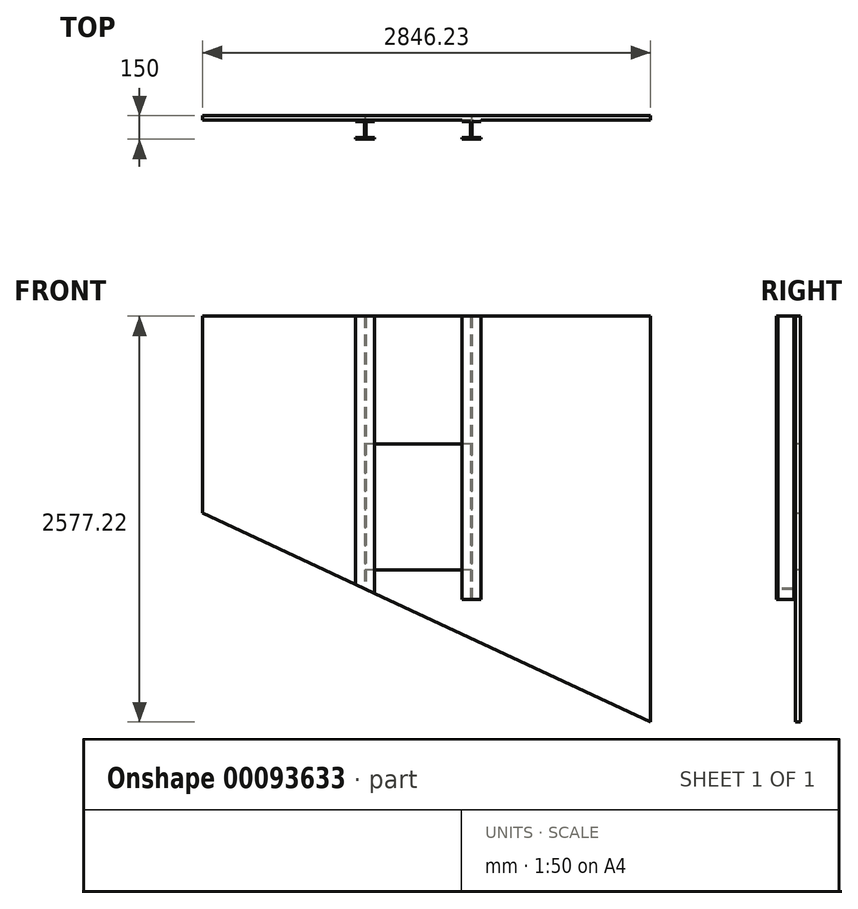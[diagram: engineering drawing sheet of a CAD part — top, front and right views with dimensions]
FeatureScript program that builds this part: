
annotation { "Feature Type Name" : "Feature", "Feature Type Description" : "" }
export const myFeature = defineFeature(function(context is Context, id is Id, definition is map)
    precondition{}
    {
        {
            var Q0;
            Q0=qCreatedBy(makeId("Top.planeOp"),FACE);
            var sketch = newSketch(context, id + "F0", { "sketchPlane" : qUnion([Q0])});
            skLineSegment(sketch, "E0.bottom", {"start": v(-5, -60) * mm, "end": v(5, -60) * mm});
            skLineSegment(sketch, "E0.top", {"start": v(-5, 60) * mm, "end": v(5, 60) * mm});
            skLineSegment(sketch, "E0.left", {"start": v(-5, -50) * mm, "end": v(-5, 50) * mm});
            skLineSegment(sketch, "E0.right", {"start": v(5, -50) * mm, "end": v(5, 50) * mm});
            skPoint(sketch, "E0.middle", {"position": v(0, 0) * mm});
            skLineSegment(sketch, "E1", {"start": v(-5, 60) * mm, "end": v(-60, 60) * mm});
            skLineSegment(sketch, "E2", {"start": v(-60, 60) * mm, "end": v(-60, 50) * mm});
            skLineSegment(sketch, "E3", {"start": v(-60, 50) * mm, "end": v(-5, 50) * mm});
            skLineSegment(sketch, "E4", {"start": v(60, 50) * mm, "end": v(60, 60) * mm});
            skLineSegment(sketch, "E5", {"start": v(60, 60) * mm, "end": v(5, 60) * mm});
            skLineSegment(sketch, "E6", {"start": v(-60, -60) * mm, "end": v(60, -60) * mm});
            skLineSegment(sketch, "E7", {"start": v(60, -60) * mm, "end": v(60, -50) * mm});
            skLineSegment(sketch, "E8", {"start": v(60, -50) * mm, "end": v(5, -50) * mm});
            skLineSegment(sketch, "E9", {"start": v(-60, -50) * mm, "end": v(-60, -60) * mm});
            skLineSegment(sketch, "E10.trimOffspring", {"start": v(5, 50) * mm, "end": v(60, 50) * mm});
            skLineSegment(sketch, "E11.trimOffspring", {"start": v(-5, -50) * mm, "end": v(-60, -50) * mm});
            skSolve(sketch);
        }
        {
            var Q0;
            Q0 = qSketchRegion(id + "F0", true);
            extrude(context, id + "F1", {"entities" : qUnion([Q0]), "depth" : 1800 * mm});
        }
        {
            var Q0;
            Q0=qCreatedBy(makeId("Right.planeOp"),FACE);
            cPlane(context, id + "F2", {"entities" : qUnion([Q0]), "cplaneType" : CPlaneType.OFFSET, "offset" : 337.5 * mm, "width" : 150 * mm, "height" : 150 * mm});
        }
        {
            var Q0;
            Q0=makeQuery(id+"F1.opExtrude","SWEPT_BODY",BODY,{"disambiguationData":[OSD([sQuery(id+"F0.wireOp",EDGE,"E0.top"),sQuery(id+"F0.wireOp",EDGE,"E0.left"),sQuery(id+"F0.wireOp",EDGE,"E0.right"),sQuery(id+"F0.wireOp",EDGE,"E1"),sQuery(id+"F0.wireOp",EDGE,"E2"),sQuery(id+"F0.wireOp",EDGE,"E3"),sQuery(id+"F0.wireOp",EDGE,"E4"),sQuery(id+"F0.wireOp",EDGE,"E5"),sQuery(id+"F0.wireOp",EDGE,"E6"),sQuery(id+"F0.wireOp",EDGE,"E7"),sQuery(id+"F0.wireOp",EDGE,"E8"),sQuery(id+"F0.wireOp",EDGE,"E9"),sQuery(id+"F0.wireOp",EDGE,"E10.trimOffspring"),sQuery(id+"F0.wireOp",EDGE,"E11.trimOffspring")])]});
            var Q1;
            Q1=qCreatedBy(id+"F2.planeOp",FACE);
            mirror(context, id + "F3", {"entities" : qUnion([Q0]), "mirrorPlane" : qUnion([Q1])});
        }
        {
            var Q0;
            Q0=makeQuery(id+"F3.opPattern","COPY",FACE,{"derivedFrom":makeQuery(id+"F1.opExtrude","SWEPT_FACE",FACE,{"disambiguationData":[OSD([sQuery(id+"F0.wireOp",EDGE,"E0.top"),sQuery(id+"F0.wireOp",EDGE,"E1"),sQuery(id+"F0.wireOp",EDGE,"E5")])]}),"instanceName":"1"});
            var sketch = newSketch(context, id + "F4", { "sketchPlane" : qUnion([Q0])});
            skLineSegment(sketch, "E12.bottom", {"start": v(-675, 1800) * mm, "end": v(-1813.73, 1800) * mm});
            skLineSegment(sketch, "E12.top", {"start": v(-675, 0) * mm, "end": v(-1813.73, 0) * mm});
            skLineSegment(sketch, "E12.left", {"start": v(-675, 987.37) * mm, "end": v(-675, 187.37) * mm});
            skLineSegment(sketch, "E12.right", {"start": v(-1813.73, 1800) * mm, "end": v(-1813.73, 0) * mm});
            skLineSegment(sketch, "E13.bottom", {"start": v(0, 1800) * mm, "end": v(1032.5, 1800) * mm});
            skLineSegment(sketch, "E13.top", {"start": v(0, 0) * mm, "end": v(1032.5, 0) * mm});
            skLineSegment(sketch, "E13.left", {"start": v(0, 987.37) * mm, "end": v(0, 187.37) * mm});
            skLineSegment(sketch, "E13.right", {"start": v(1032.5, 1800) * mm, "end": v(1032.5, 0) * mm});
            skLineSegment(sketch, "E14.bottom", {"start": v(-675, 0) * mm, "end": v(0, 0) * mm});
            skLineSegment(sketch, "E14.top", {"start": v(-675, 187.37) * mm, "end": v(0, 187.37) * mm});
            skLineSegment(sketch, "E15.bottom", {"start": v(-675, 1800) * mm, "end": v(0, 1800) * mm});
            skLineSegment(sketch, "E15.top", {"start": v(-675, 987.37) * mm, "end": v(0, 987.37) * mm});
            skSolve(sketch);
        }
        {
            var Q0;
            Q0 = qSketchRegion(id + "F4", true);
            extrude(context, id + "F5", {"entities" : qUnion([Q0]), "depth" : 30 * mm});
        }
        {
            var Q0;
            Q0=makeQuery(id+"F5.opExtrude","CAP_FACE",FACE,{"disambiguationData":[OSD([sQuery(id+"F4.wireOp",EDGE,"E12.bottom"),sQuery(id+"F4.wireOp",EDGE,"E12.top"),sQuery(id+"F4.wireOp",EDGE,"E12.left"),sQuery(id+"F4.wireOp",EDGE,"E12.right"),sQuery(id+"F4.wireOp",EDGE,"E13.bottom"),sQuery(id+"F4.wireOp",EDGE,"E13.top"),sQuery(id+"F4.wireOp",EDGE,"E13.left"),sQuery(id+"F4.wireOp",EDGE,"E13.right"),sQuery(id+"F4.wireOp",EDGE,"E14.bottom"),sQuery(id+"F4.wireOp",EDGE,"E14.top"),sQuery(id+"F4.wireOp",EDGE,"E15.bottom"),sQuery(id+"F4.wireOp",EDGE,"E15.top")])],"isStart":false});
            var sketch = newSketch(context, id + "F6", { "sketchPlane" : qUnion([Q0])});
            skLineSegment(sketch, "E16", {"start": v(1032.5, 550) * mm, "end": v(-1813.73, -777.22) * mm});
            skLineSegment(sketch, "E17", {"start": v(-1813.73, -777.22) * mm, "end": v(-1813.73, 0) * mm});
            skLineSegment(sketch, "E18", {"start": v(-1813.73, 0) * mm, "end": v(-146.98, 0) * mm});
            skSolve(sketch);
        }
        {
            var Q0;
            Q0 = qSketchRegion(id + "F6", true);
            extrude(context, id + "F7", {"entities" : qUnion([Q0]), "operationType" : NewBodyOperationType.ADD, "oppositeDirection" : true, "depth" : 30 * mm});
        }
        {
            var Q0;
            Q0=makeQuery(id+"F7.boolean.opBoolean","MERGE",FACE,{"derivedFrom":[makeQuery(id+"F5.opExtrude","CAP_FACE",FACE,{"disambiguationData":[OSD([sQuery(id+"F4.wireOp",EDGE,"E12.bottom"),sQuery(id+"F4.wireOp",EDGE,"E12.top"),sQuery(id+"F4.wireOp",EDGE,"E12.left"),sQuery(id+"F4.wireOp",EDGE,"E12.right"),sQuery(id+"F4.wireOp",EDGE,"E13.bottom"),sQuery(id+"F4.wireOp",EDGE,"E13.top"),sQuery(id+"F4.wireOp",EDGE,"E13.left"),sQuery(id+"F4.wireOp",EDGE,"E13.right"),sQuery(id+"F4.wireOp",EDGE,"E14.bottom"),sQuery(id+"F4.wireOp",EDGE,"E14.top"),sQuery(id+"F4.wireOp",EDGE,"E15.bottom"),sQuery(id+"F4.wireOp",EDGE,"E15.top")])],"isStart":false}),makeQuery(id+"F7.opExtrude","CAP_FACE",FACE,{"disambiguationData":[OSD([sQuery(id+"F6.wireOp",EDGE,"E16"),sQuery(id+"F6.wireOp",EDGE,"E17"),sQuery(id+"F6.wireOp",EDGE,"E18")])],"isStart":true})]});
            var sketch = newSketch(context, id + "F8", { "sketchPlane" : qUnion([Q0])});
            skLineSegment(sketch, "E19", {"start": v(-146.98, 0) * mm, "end": v(1032.5, 550) * mm});
            skLineSegment(sketch, "E20", {"start": v(1032.5, 550) * mm, "end": v(1032.5, 0) * mm});
            skLineSegment(sketch, "E21", {"start": v(1032.5, 0) * mm, "end": v(-146.98, 0) * mm});
            skSolve(sketch);
        }
        {
            var Q0;
            Q0 = qSketchRegion(id + "F8", true);
            extrude(context, id + "F9", {"entities" : qUnion([Q0]), "operationType" : NewBodyOperationType.REMOVE, "oppositeDirection" : true, "depth" : 1003 * mm});
        }
    });
